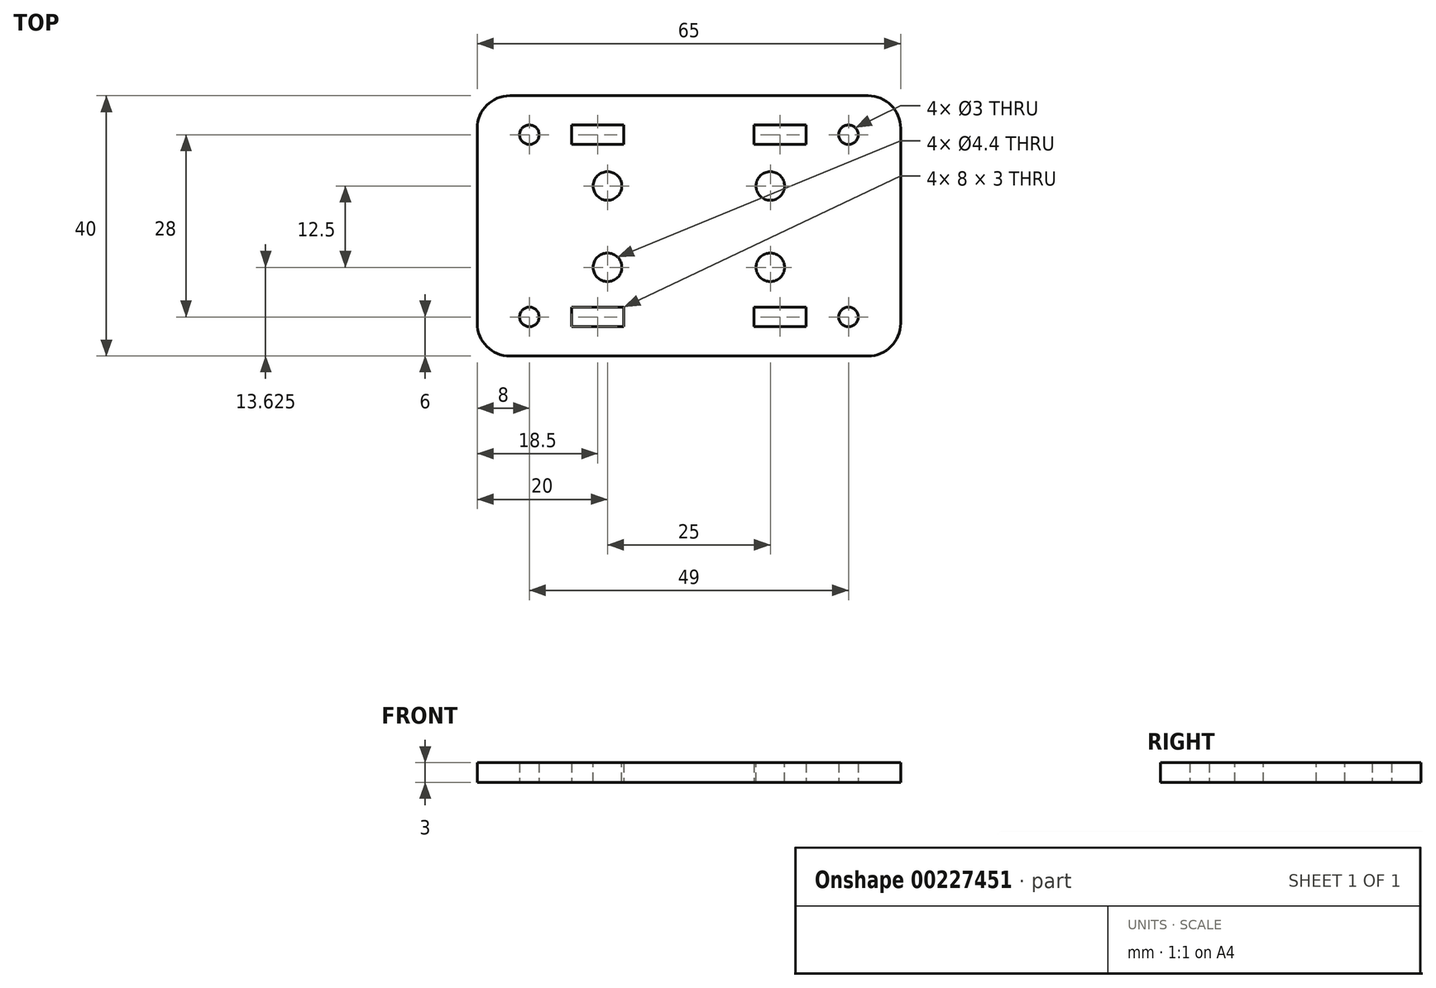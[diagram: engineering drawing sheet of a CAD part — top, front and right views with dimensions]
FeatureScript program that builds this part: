
annotation { "Feature Type Name" : "Feature", "Feature Type Description" : "" }
export const myFeature = defineFeature(function(context is Context, id is Id, definition is map)
    precondition{}
    {
        {
            assignVariable(context, id + "F0", {"name" : "Thickness", "anyValue" : 3});
        }
        {
            var Q0;
            Q0=qCreatedBy(makeId("Top.planeOp"),FACE);
            var sketch = newSketch(context, id + "F1", { "sketchPlane" : qUnion([Q0])});
            skLineSegment(sketch, "E0.bottom", {"start": v(32.5, -20) * mm, "end": v(-32.5, -20) * mm});
            skLineSegment(sketch, "E0.top", {"start": v(32.5, 20) * mm, "end": v(-32.5, 20) * mm});
            skLineSegment(sketch, "E0.left", {"start": v(32.5, -20) * mm, "end": v(32.5, 20) * mm});
            skLineSegment(sketch, "E0.right", {"start": v(-32.5, -20) * mm, "end": v(-32.5, 20) * mm});
            skPoint(sketch, "E0.middle", {"position": v(0, 0) * mm});
            skLineSegment(sketch, "E1", {"start": v(-32.5, -14) * mm, "end": v(32.5, -14) * mm, "construction": true});
            skPoint(sketch, "E2", {"position": v(-14, -14) * mm});
            skLineSegment(sketch, "E3.bottom", {"start": v(-10, -15.5) * mm, "end": v(-18, -15.5) * mm});
            skLineSegment(sketch, "E3.top", {"start": v(-10, -12.5) * mm, "end": v(-18, -12.5) * mm});
            skLineSegment(sketch, "E3.left", {"start": v(-10, -15.5) * mm, "end": v(-10, -12.5) * mm});
            skLineSegment(sketch, "E3.right", {"start": v(-18, -15.5) * mm, "end": v(-18, -12.5) * mm});
            skPoint(sketch, "E4.MirrorP", {"position": v(14, -14) * mm});
            skLineSegment(sketch, "E5.MirrorCS", {"start": v(18, -15.5) * mm, "end": v(18, -12.5) * mm});
            skLineSegment(sketch, "E6.MirrorCS", {"start": v(10, -15.5) * mm, "end": v(10, -12.5) * mm});
            skLineSegment(sketch, "E7.MirrorCS", {"start": v(10, -12.5) * mm, "end": v(18, -12.5) * mm});
            skLineSegment(sketch, "E8.MirrorCS", {"start": v(10, -15.5) * mm, "end": v(18, -15.5) * mm});
            skPoint(sketch, "E9.MirrorP", {"position": v(14, 14) * mm});
            skPoint(sketch, "E10.MirrorP", {"position": v(-14, 14) * mm});
            skLineSegment(sketch, "E11.MirrorCS", {"start": v(-10, 12.5) * mm, "end": v(-18, 12.5) * mm});
            skLineSegment(sketch, "E12.MirrorCS", {"start": v(-10, 15.5) * mm, "end": v(-10, 12.5) * mm});
            skLineSegment(sketch, "E13.MirrorCS", {"start": v(-18, 15.5) * mm, "end": v(-18, 12.5) * mm});
            skLineSegment(sketch, "E14.MirrorCS", {"start": v(18, 15.5) * mm, "end": v(18, 12.5) * mm});
            skLineSegment(sketch, "E15.MirrorCS", {"start": v(-10, 15.5) * mm, "end": v(-18, 15.5) * mm});
            skLineSegment(sketch, "E16.MirrorCS", {"start": v(10, 15.5) * mm, "end": v(18, 15.5) * mm});
            skLineSegment(sketch, "E17.MirrorCS", {"start": v(10, 15.5) * mm, "end": v(10, 12.5) * mm});
            skLineSegment(sketch, "E18.MirrorCS", {"start": v(10, 12.5) * mm, "end": v(18, 12.5) * mm});
            skCircle(sketch, "E19", {"center": v(-24.5, -14) * mm, "radius": 1.5 * mm});
            skCircle(sketch, "E20.MirrorC", {"center": v(24.5, -14) * mm, "radius": 1.5 * mm});
            skCircle(sketch, "E21.MirrorC", {"center": v(-24.5, 14) * mm, "radius": 1.5 * mm});
            skCircle(sketch, "E22.MirrorC", {"center": v(24.5, 14) * mm, "radius": 1.5 * mm});
            skSolve(sketch);
        }
        {
            var Q0;
            Q0=makeQuery(id+"F1.imprint","IMPRINT",FACE,{"disambiguationData":[TD([[makeQuery(id+"F1.imprint","IMPRINT",EDGE,{"derivedFrom":sQuery(id+"F1.wireOp",EDGE,"E0.bottom")}),-1.0]])]});
            extrude(context, id + "F2", {"entities" : qUnion([Q0]), "depth" : (getVariable(context, 'Thickness')) * mm});
        }
        {
            var Q0;
            Q0=makeQuery(id+"F2.opExtrude","SWEPT_EDGE",EDGE,{"disambiguationData":[OSD([sQuery(id+"F1.wireOp",EDGE,"E0.bottom"),sQuery(id+"F1.wireOp",EDGE,"E0.right")])]});
            var Q1;
            Q1=makeQuery(id+"F2.opExtrude","SWEPT_EDGE",EDGE,{"disambiguationData":[OSD([sQuery(id+"F1.wireOp",EDGE,"E0.top"),sQuery(id+"F1.wireOp",EDGE,"E0.right")])]});
            var Q2;
            Q2=makeQuery(id+"F2.opExtrude","SWEPT_EDGE",EDGE,{"disambiguationData":[OSD([sQuery(id+"F1.wireOp",EDGE,"E0.bottom"),sQuery(id+"F1.wireOp",EDGE,"E0.left")])]});
            var Q3;
            Q3=makeQuery(id+"F2.opExtrude","SWEPT_EDGE",EDGE,{"disambiguationData":[OSD([sQuery(id+"F1.wireOp",EDGE,"E0.top"),sQuery(id+"F1.wireOp",EDGE,"E0.left")])]});
            fillet(context, id + "F3", {"entities" : qUnion([Q0, Q1, Q2, Q3]), "radius" : 5 * mm, "tangentPropagation" : true, "allowEdgeOverflow" : false});
        }
        {
            var Q0;
            Q0=makeQuery(id+"F2.opExtrude","CAP_FACE",FACE,{"disambiguationData":[OSD([sQuery(id+"F1.wireOp",EDGE,"E0.bottom"),sQuery(id+"F1.wireOp",EDGE,"E0.top"),sQuery(id+"F1.wireOp",EDGE,"E0.left"),sQuery(id+"F1.wireOp",EDGE,"E0.right"),sQuery(id+"F1.wireOp",EDGE,"E3.bottom"),sQuery(id+"F1.wireOp",EDGE,"E3.top"),sQuery(id+"F1.wireOp",EDGE,"E3.left"),sQuery(id+"F1.wireOp",EDGE,"E3.right"),sQuery(id+"F1.wireOp",EDGE,"E5.MirrorCS"),sQuery(id+"F1.wireOp",EDGE,"E6.MirrorCS"),sQuery(id+"F1.wireOp",EDGE,"E7.MirrorCS"),sQuery(id+"F1.wireOp",EDGE,"E8.MirrorCS"),sQuery(id+"F1.wireOp",EDGE,"E11.MirrorCS"),sQuery(id+"F1.wireOp",EDGE,"E12.MirrorCS"),sQuery(id+"F1.wireOp",EDGE,"E13.MirrorCS"),sQuery(id+"F1.wireOp",EDGE,"E14.MirrorCS"),sQuery(id+"F1.wireOp",EDGE,"E15.MirrorCS"),sQuery(id+"F1.wireOp",EDGE,"E16.MirrorCS"),sQuery(id+"F1.wireOp",EDGE,"E17.MirrorCS"),sQuery(id+"F1.wireOp",EDGE,"E18.MirrorCS"),sQuery(id+"F1.wireOp",EDGE,"E19"),sQuery(id+"F1.wireOp",EDGE,"E20.MirrorC"),sQuery(id+"F1.wireOp",EDGE,"E21.MirrorC"),sQuery(id+"F1.wireOp",EDGE,"E22.MirrorC")])],"isStart":false});
            var sketch = newSketch(context, id + "F4", { "sketchPlane" : qUnion([Q0])});
            skPoint(sketch, "E23", {"position": v(-12.5, 6.12) * mm});
            skPoint(sketch, "E24.0.1.0", {"position": v(-12.5, -6.38) * mm});
            skPoint(sketch, "E24.1.0.0", {"position": v(12.5, 6.12) * mm});
            skPoint(sketch, "E24.1.1.0", {"position": v(12.5, -6.38) * mm});
            skLineSegment(sketch, "E24.direction1", {"start": v(-12.5, 6.12) * mm, "end": v(12.5, 6.12) * mm, "construction": true});
            skLineSegment(sketch, "E24.direction2", {"start": v(-12.5, 6.12) * mm, "end": v(-12.5, -6.37) * mm, "construction": true});
            skSolve(sketch);
        }
        {
            var Q0;
            Q0=sQuery(id+"F4.wireOp",VERTEX,"E23");
            var Q1;
            Q1=sQuery(id+"F4.wireOp",VERTEX,"E24.0.1.0");
            var Q2;
            Q2=sQuery(id+"F4.wireOp",VERTEX,"E24.1.0.0");
            var Q3;
            Q3=sQuery(id+"F4.wireOp",VERTEX,"E24.1.1.0");
            var Q4;
            Q4=makeQuery(id+"F2.opExtrude","SWEPT_BODY",BODY,{"disambiguationData":[OSD([sQuery(id+"F1.wireOp",EDGE,"E0.bottom"),sQuery(id+"F1.wireOp",EDGE,"E0.top"),sQuery(id+"F1.wireOp",EDGE,"E0.left"),sQuery(id+"F1.wireOp",EDGE,"E0.right"),sQuery(id+"F1.wireOp",EDGE,"E3.bottom"),sQuery(id+"F1.wireOp",EDGE,"E3.top"),sQuery(id+"F1.wireOp",EDGE,"E3.left"),sQuery(id+"F1.wireOp",EDGE,"E3.right"),sQuery(id+"F1.wireOp",EDGE,"E5.MirrorCS"),sQuery(id+"F1.wireOp",EDGE,"E6.MirrorCS"),sQuery(id+"F1.wireOp",EDGE,"E7.MirrorCS"),sQuery(id+"F1.wireOp",EDGE,"E8.MirrorCS"),sQuery(id+"F1.wireOp",EDGE,"E11.MirrorCS"),sQuery(id+"F1.wireOp",EDGE,"E12.MirrorCS"),sQuery(id+"F1.wireOp",EDGE,"E13.MirrorCS"),sQuery(id+"F1.wireOp",EDGE,"E14.MirrorCS"),sQuery(id+"F1.wireOp",EDGE,"E15.MirrorCS"),sQuery(id+"F1.wireOp",EDGE,"E16.MirrorCS"),sQuery(id+"F1.wireOp",EDGE,"E17.MirrorCS"),sQuery(id+"F1.wireOp",EDGE,"E18.MirrorCS"),sQuery(id+"F1.wireOp",EDGE,"E19"),sQuery(id+"F1.wireOp",EDGE,"E20.MirrorC"),sQuery(id+"F1.wireOp",EDGE,"E21.MirrorC"),sQuery(id+"F1.wireOp",EDGE,"E22.MirrorC")])]});
            hole(context, id + "F5", {"style" : HoleStyle.SIMPLE, "endStyle" : HoleEndStyle.THROUGH, "standardTappedOrClearance" : lookupTablePath({ "standard" : "ISO", "fit" : "Normal", "size" : "M4", "type" : "Clearance" }), "standardBlindInLast" : lookupTablePath({ "fit" : "Standard", "standard" : "ISO", "size" : "M4", "type" : "Clearance" }), "holeDiameter" : 4.4 * mm, "tappedDepth" : 12 * mm, "tapClearance" : 3, "locations" : qUnion([Q0, Q1, Q2, Q3]), "scope" : qUnion([Q4])});
        }
    });
